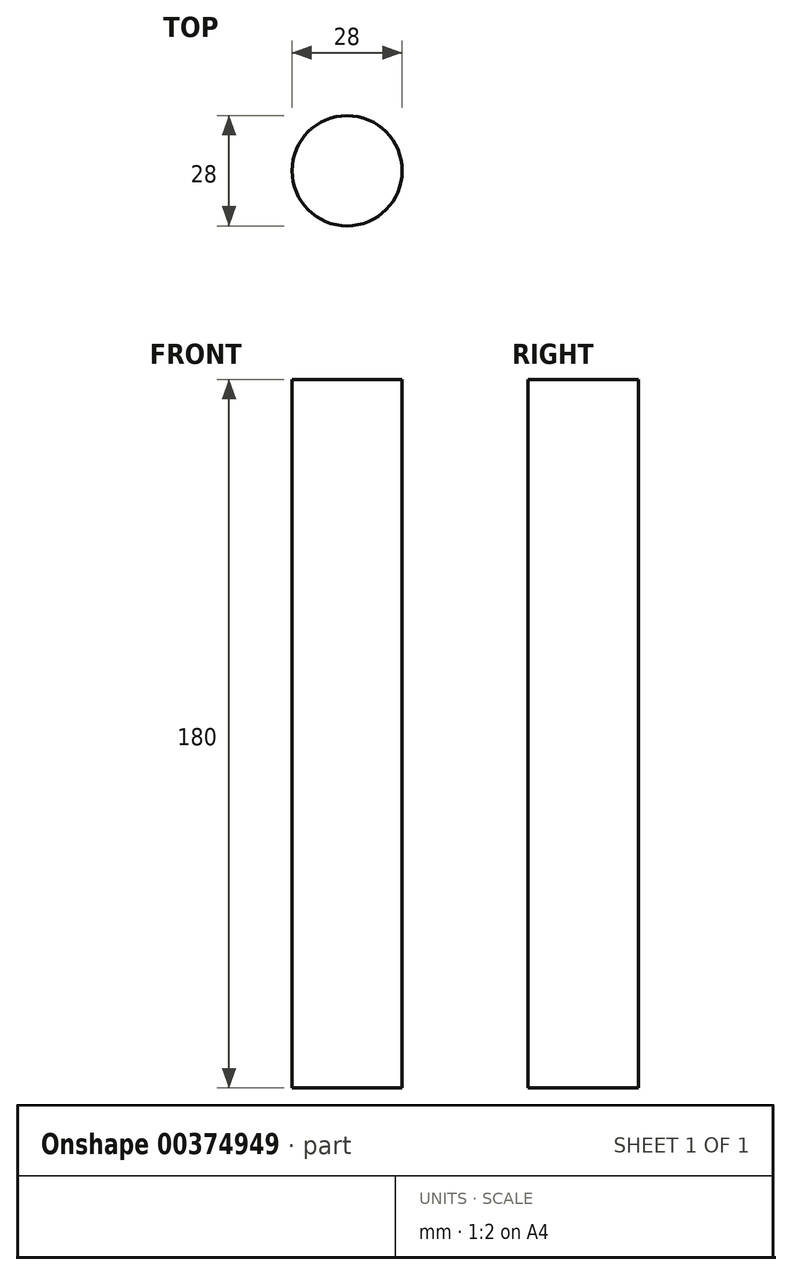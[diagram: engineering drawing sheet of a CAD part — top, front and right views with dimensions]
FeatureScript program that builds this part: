
annotation { "Feature Type Name" : "Feature", "Feature Type Description" : "" }
export const myFeature = defineFeature(function(context is Context, id is Id, definition is map)
    precondition{}
    {
        {
            var Q0;
            Q0=qCreatedBy(makeId("Top.planeOp"),FACE);
            var sketch = newSketch(context, id + "F0", { "sketchPlane" : qUnion([Q0])});
            skCircle(sketch, "E0", {"center": v(0, 0) * mm, "radius": 14 * mm});
            skSolve(sketch);
        }
        {
            var Q0;
            Q0 = qSketchRegion(id + "F0", true);
            extrude(context, id + "F1", {"entities" : qUnion([Q0]), "endBound" : BoundingType.SYMMETRIC, "depth" : 180 * mm});
        }
    });
